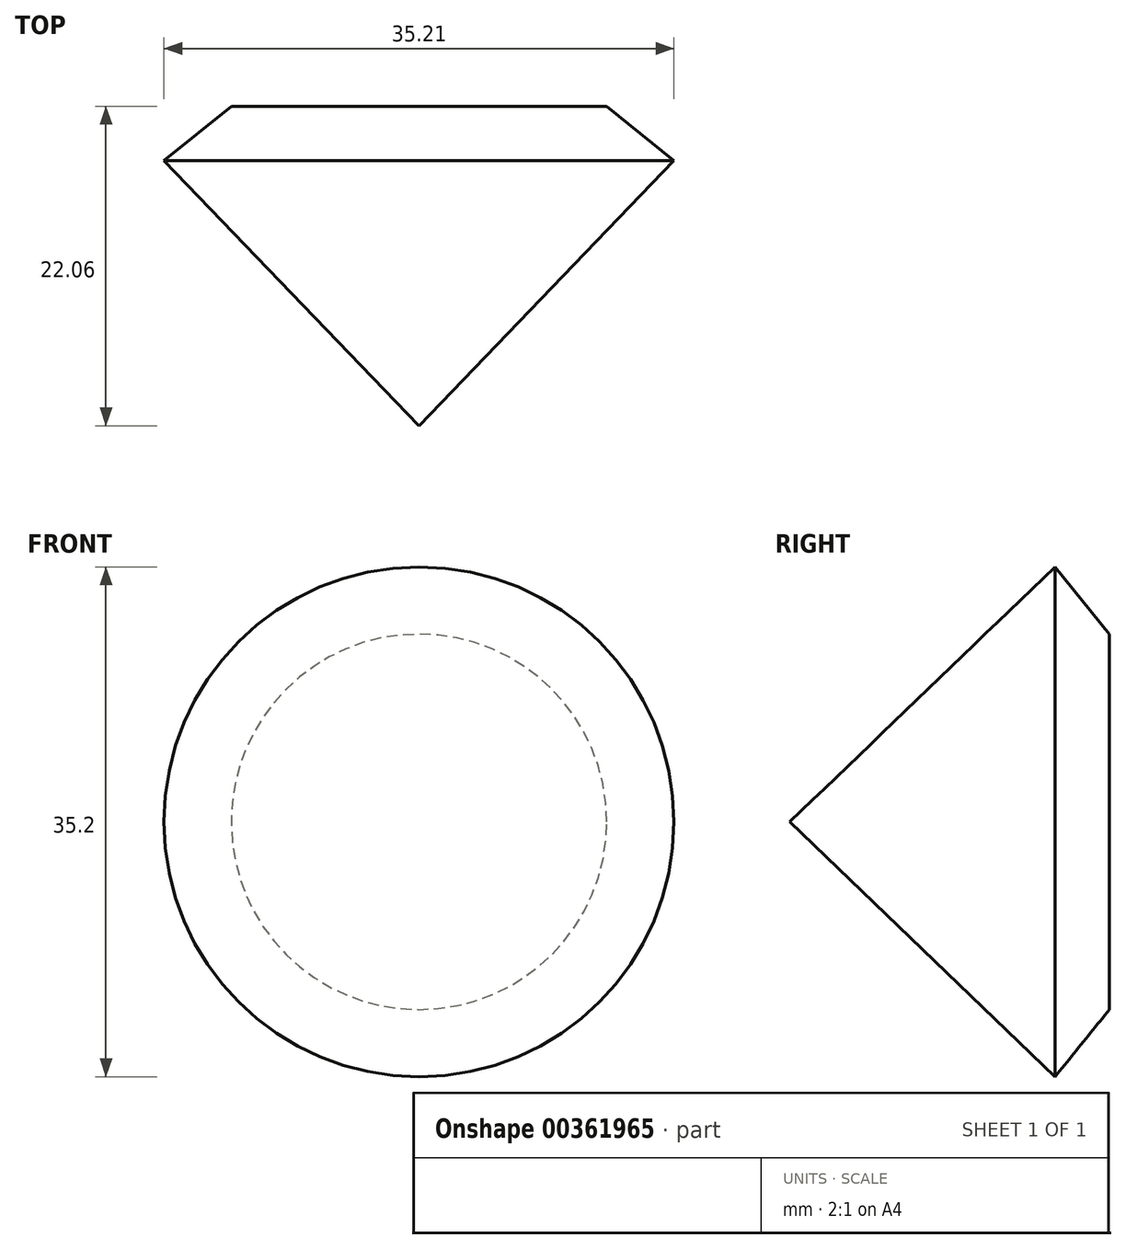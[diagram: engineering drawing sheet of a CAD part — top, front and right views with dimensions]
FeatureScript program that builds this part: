
annotation { "Feature Type Name" : "Feature", "Feature Type Description" : "" }
export const myFeature = defineFeature(function(context is Context, id is Id, definition is map)
    precondition{}
    {
        {
            var Q0;
            Q0=qCreatedBy(makeId("Top.planeOp"),FACE);
            var sketch = newSketch(context, id + "F0", { "sketchPlane" : qUnion([Q0])});
            skLineSegment(sketch, "E0", {"start": v(-12.4, 22.03) * mm, "end": v(13, 22.03) * mm});
            skLineSegment(sketch, "E1", {"start": v(13, 22.03) * mm, "end": v(17.65, 18.28) * mm});
            skLineSegment(sketch, "E2", {"start": v(17.65, 18.28) * mm, "end": v(0.05, -0.03) * mm});
            skLineSegment(sketch, "E3", {"start": v(0.05, -0.03) * mm, "end": v(0.05, 22.03) * mm});
            skSolve(sketch);
        }
        {
            var Q0;
            {var subQ0=sQuery(id+"F0.wireOp",EDGE,"E1");Q0=makeQuery(id+"F0.imprint","IMPRINT",FACE,{"disambiguationData":[TD([[makeQuery(id+"F0.imprint","IMPRINT",EDGE,{"derivedFrom":subQ0}),-1.0]])]});}
            var Q1;
            Q1=sQuery(id+"F0.wireOp",EDGE,"E3");
            revolve(context, id + "F1", {"entities" : qUnion([Q0]), "axis" : qUnion([Q1]), "revolveType" : RevolveType.FULL});
        }
    });
